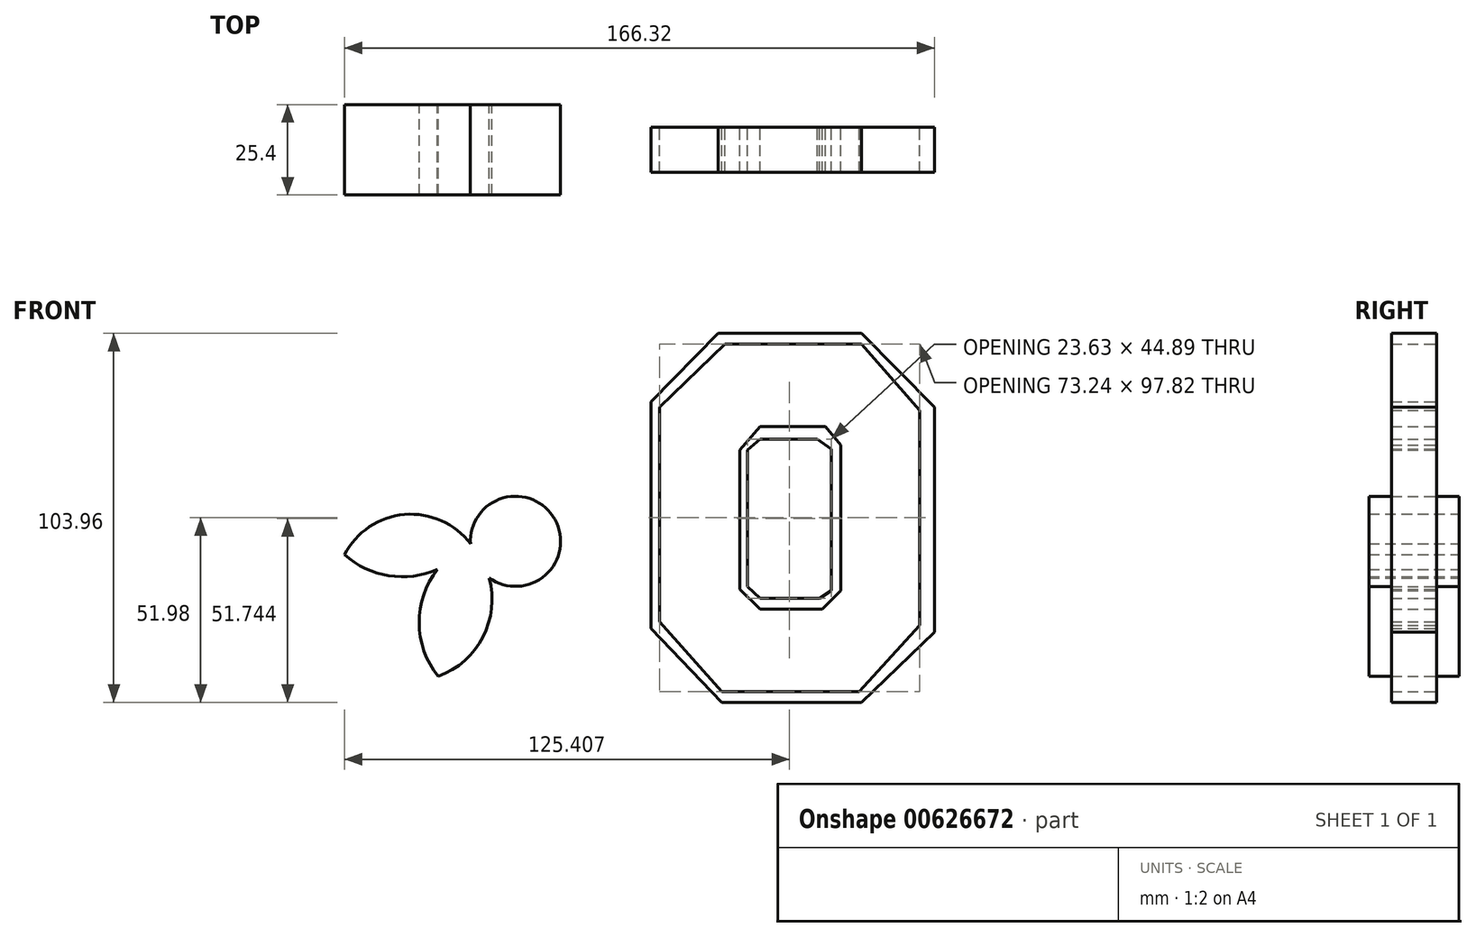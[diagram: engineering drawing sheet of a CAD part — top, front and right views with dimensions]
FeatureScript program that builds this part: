
annotation { "Feature Type Name" : "Feature", "Feature Type Description" : "" }
export const myFeature = defineFeature(function(context is Context, id is Id, definition is map)
    precondition{}
    {
        {
            var Q0;
            Q0=qCreatedBy(makeId("Front.planeOp"),FACE);
            var sketch = newSketch(context, id + "F0", { "sketchPlane" : qUnion([Q0])});
            skLineSegment(sketch, "E0", {"start": v(2.22, 18.7) * mm, "end": v(2.22, -19.81) * mm});
            skLineSegment(sketch, "E1", {"start": v(2.22, -19.81) * mm, "end": v(5.77, -23.12) * mm});
            skLineSegment(sketch, "E2", {"start": v(5.77, -23.12) * mm, "end": v(22.54, -23.12) * mm});
            skLineSegment(sketch, "E3", {"start": v(22.54, -23.12) * mm, "end": v(25.85, -21) * mm});
            skLineSegment(sketch, "E4", {"start": v(25.85, -21) * mm, "end": v(25.85, 18.93) * mm});
            skLineSegment(sketch, "E5", {"start": v(25.85, 18.93) * mm, "end": v(21.83, 21.77) * mm});
            skLineSegment(sketch, "E6", {"start": v(21.83, 21.77) * mm, "end": v(5.77, 21.77) * mm});
            skLineSegment(sketch, "E7", {"start": v(5.77, 21.77) * mm, "end": v(2.22, 18.7) * mm});
            skLineSegment(sketch, "E8", {"start": v(0, 18.7) * mm, "end": v(0, -20.52) * mm});
            skLineSegment(sketch, "E9", {"start": v(0, -20.52) * mm, "end": v(5.77, -26.2) * mm});
            skLineSegment(sketch, "E10", {"start": v(5.77, -26.2) * mm, "end": v(23.25, -26.2) * mm});
            skLineSegment(sketch, "E11", {"start": v(23.25, -26.2) * mm, "end": v(28.45, -21) * mm});
            skLineSegment(sketch, "E12", {"start": v(28.45, -21) * mm, "end": v(28.45, 20.12) * mm});
            skLineSegment(sketch, "E13", {"start": v(28.45, 20.12) * mm, "end": v(24.2, 25.31) * mm});
            skLineSegment(sketch, "E14", {"start": v(24.2, 25.31) * mm, "end": v(5.77, 25.31) * mm});
            skLineSegment(sketch, "E15", {"start": v(5.77, 25.31) * mm, "end": v(0, 18.7) * mm});
            skLineSegment(sketch, "E16", {"start": v(-2.97, 21.77) * mm, "end": v(-2.97, -23.83) * mm});
            skLineSegment(sketch, "E17", {"start": v(-2.97, -23.83) * mm, "end": v(2.22, -28.8) * mm});
            skLineSegment(sketch, "E18", {"start": v(2.22, -28.8) * mm, "end": v(24.9, -28.8) * mm});
            skLineSegment(sketch, "E19", {"start": v(24.9, -28.8) * mm, "end": v(31.05, -22.89) * mm});
            skLineSegment(sketch, "E20", {"start": v(31.05, -22.89) * mm, "end": v(31.05, 21.77) * mm});
            skLineSegment(sketch, "E21", {"start": v(31.05, 21.77) * mm, "end": v(24.9, 27.91) * mm});
            skLineSegment(sketch, "E22", {"start": v(24.9, 27.91) * mm, "end": v(3.88, 27.91) * mm});
            skLineSegment(sketch, "E23", {"start": v(3.88, 27.91) * mm, "end": v(-2.97, 21.77) * mm});
            skLineSegment(sketch, "E24", {"start": v(-19.51, 27.91) * mm, "end": v(-19.51, -29.26) * mm});
            skLineSegment(sketch, "E25", {"start": v(-19.51, -29.26) * mm, "end": v(-2.97, -45.8) * mm});
            skLineSegment(sketch, "E26", {"start": v(-2.97, -45.8) * mm, "end": v(32, -45.8) * mm});
            skLineSegment(sketch, "E27", {"start": v(32, -45.8) * mm, "end": v(47.82, -29.74) * mm});
            skLineSegment(sketch, "E28", {"start": v(47.82, -29.74) * mm, "end": v(47.82, 30.04) * mm});
            skLineSegment(sketch, "E29", {"start": v(47.82, 30.04) * mm, "end": v(32.94, 44.69) * mm});
            skLineSegment(sketch, "E30", {"start": v(32.94, 44.69) * mm, "end": v(-2.97, 44.69) * mm});
            skLineSegment(sketch, "E31", {"start": v(-2.97, 44.69) * mm, "end": v(-19.51, 27.91) * mm});
            skLineSegment(sketch, "E32", {"start": v(-22.58, 30.75) * mm, "end": v(-22.58, -29.74) * mm});
            skLineSegment(sketch, "E33", {"start": v(-22.58, -29.74) * mm, "end": v(-5.1, -49.35) * mm});
            skLineSegment(sketch, "E34", {"start": v(-5.1, -49.35) * mm, "end": v(33.65, -49.35) * mm});
            skLineSegment(sketch, "E35", {"start": v(33.65, -49.35) * mm, "end": v(50.66, -30.68) * mm});
            skLineSegment(sketch, "E36", {"start": v(50.66, -30.68) * mm, "end": v(50.66, 29.8) * mm});
            skLineSegment(sketch, "E37", {"start": v(50.66, 29.8) * mm, "end": v(34.36, 48.47) * mm});
            skLineSegment(sketch, "E38", {"start": v(34.36, 48.47) * mm, "end": v(-4.16, 48.47) * mm});
            skLineSegment(sketch, "E39", {"start": v(-4.16, 48.47) * mm, "end": v(-22.58, 30.75) * mm});
            skLineSegment(sketch, "E40", {"start": v(-6.05, 51.54) * mm, "end": v(-25.02, 32.26) * mm});
            skLineSegment(sketch, "E41", {"start": v(-25.02, 32.26) * mm, "end": v(-25.02, -31.63) * mm});
            skLineSegment(sketch, "E42", {"start": v(-25.02, -31.63) * mm, "end": v(-5.03, -52.42) * mm});
            skLineSegment(sketch, "E43", {"start": v(-5.03, -52.42) * mm, "end": v(34.36, -52.42) * mm});
            skLineSegment(sketch, "E44", {"start": v(34.36, -52.42) * mm, "end": v(54.95, -32.62) * mm});
            skLineSegment(sketch, "E45", {"start": v(54.95, -32.62) * mm, "end": v(54.95, 30.75) * mm});
            skLineSegment(sketch, "E46", {"start": v(54.95, 30.75) * mm, "end": v(34.36, 51.54) * mm});
            skLineSegment(sketch, "E47", {"start": v(34.36, 51.54) * mm, "end": v(-6.05, 51.54) * mm});
            skSolve(sketch);
        }
        {
            var Q0;
            Q0 = qSketchRegion(id + "F0", true);
            extrude(context, id + "F1", {"entities" : qUnion([Q0]), "depth" : 12.7 * mm, "offsetDistance" : 25.4 * mm, "symmetric" : true});
        }
        {
            var Q0;
            Q0=makeQuery(id+"F0.imprint","IMPRINT",FACE,{"disambiguationData":[TD([[makeQuery(id+"F0.imprint","IMPRINT",EDGE,{"derivedFrom":sQuery(id+"F0.wireOp",EDGE,"E0")}),-1.0]])]});
            var sketch = newSketch(context, id + "F2", { "sketchPlane" : qUnion([Q0])});
            skSolve(sketch);
        }
        {
            var Q0;
            Q0 = qSketchRegion(id + "F2", true);
            var Q1;
            Q1=makeQuery(id+"F0.imprint","IMPRINT",FACE,{"disambiguationData":[TD([[makeQuery(id+"F0.imprint","IMPRINT",EDGE,{"derivedFrom":sQuery(id+"F0.wireOp",EDGE,"E0")}),-1.0]])]});
            extrude(context, id + "F3", {"entities" : qUnion([Q0, Q1]), "depth" : 12.7 * mm, "offsetDistance" : 25.4 * mm, "symmetric" : true});
        }
        {
            var Q0;
            Q0=qCreatedBy(makeId("Front.planeOp"),FACE);
            var sketch = newSketch(context, id + "F4", { "sketchPlane" : qUnion([Q0])});
            skCircle(sketch, "E48", {"center": v(-63.17, -7.06) * mm, "radius": 12.7 * mm});
            skArc(sketch, "E49", {"start": v(-75.85, -7.8) * mm, "mid": v(-89.64, -24.2) * mm, "end": v(-84.9, -45.1) * mm});
            skArc(sketch, "E50", {"start": v(-84.9, -45.1) * mm, "mid": v(-70.44, -28.86) * mm, "end": v(-75.85, -7.8) * mm});
            skArc(sketch, "E51", {"start": v(-111.37, -10.84) * mm, "mid": v(-92.96, -16.95) * mm, "end": v(-75.85, -7.8) * mm});
            skArc(sketch, "E52", {"start": v(-75.85, -7.8) * mm, "mid": v(-94.45, 0.5) * mm, "end": v(-111.37, -10.84) * mm});
            skSolve(sketch);
        }
        {
            var Q0;
            Q0 = qSketchRegion(id + "F4", true);
            extrude(context, id + "F5", {"entities" : qUnion([Q0]), "depth" : 25.4 * mm, "offsetDistance" : 25.4 * mm, "symmetric" : true});
        }
    });
